# Revit family: NLRS_33_GM_FB_TC_STORAX_vloerluik_BV-FL_BCB
name_source: partatom
category: Generic Models
revit_build: Autodesk Revit 2014 (Build: 20130308_1515(x64)
units: mm (PartAtom-declared; Revit-internal decimal feet)

## types (6) — shared parameters
Default Elevation = 1219 mm
Manufacturer = Storax
Model = BV
URL = http://www.storax.nl
belasting = 15 kN
binnenluik = tbv betonvulling
brandwerend 90 min = nee
gasdrukveer = nee
geïsoleerd = nee
materiaal = bcb_staal
productgroep = Vloerluiken
rubberen_afdichting = enkel
scharnierend = nee
sluiting = 4
vergrendeling = nee
vullen_met_beton = ja

## per-type parameters (varying)
| type | binnenmaat_breedte | binnenmaat_lengte | gewicht | uitwendige_breedte | uitwendige_lengte |
| maatwerk | 305 mm | 305 mm | 10 | 435 mm | 435 mm |
| BV-FL 55 | 500 mm | 500 mm | 17 | 630 mm | 630 mm |
| BV-FL 64 | 400 mm  [stored 1.31234 ft] | 600 mm | 17 | 530 mm | 730 mm |
| BV-FL 66 | 600 mm | 600 mm | 21 | 730 mm | 730 mm |
| BV-FL 86 | 600 mm | 800 mm | 27 | 730 mm | 930 mm  [stored 3.05118 ft] |
| BV-FL 88 | 800 mm | 800 mm | 31 | 930 mm  [stored 3.05118 ft] | 930 mm  [stored 3.05118 ft] |

note: [stored X ft] marks values corroborated as IEEE doubles in the binary element streams (Revit-internal decimal feet)

## geometry (parser evidence)
native form markers: Blend x811, Sweep x7
no freeform markers — native parametric forms only
